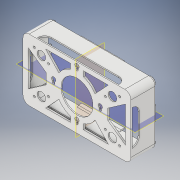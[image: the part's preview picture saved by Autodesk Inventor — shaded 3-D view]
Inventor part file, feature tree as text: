
AUTODESK INVENTOR PART (.ipt)
format: ipt  version: 2018 (Build 220112000, 112)  size: 521,216 bytes
history: native  units: in
note: dims shown in document units (in); Inventor stores cm internally (conversion verified against a paired STEP export)
features: extrude x8, sketch x8, projected_geometry x4, reference x4, other x4, plane x2, chamfer x2, mirror x2
ambient origin geometry x8: Origin, YZ Plane, XZ Plane, XY Plane, X Axis, Y Axis, Z Axis, Center Point
bodies: Solid1 (feature_tree)
feature tree (34):
  extrude  "Extrusion1"  Depth=0.0827in TaperAngle=0.0deg
  sketch  "Sketch4"  dims[d103=0.15in d104=0.0799in]
  extrude  "Extrusion12"  Depth=0.0799in
  sketch  "Sketch7"  dims[d105=0.2299in d106=1.64in]
  extrude  "Extrusion14"  Depth=1.64in
  extrude  "Extrusion16"  Depth=0.15in
  extrude  "Extrusion17"  Depth=3.28in
  plane  "Work Plane4"
  plane  "Work Plane5"
  extrude  "Extrusion23"  Depth=3.28in
  chamfer  "Chamfer2"  Distance=0.3937in
  chamfer  "Chamfer3"  Distance=1.0in
  extrude  "Extrusion24"  Depth=0.5in
  mirror  "Mirror3"
  extrude  "Extrusion25"  Depth=0.5in
  mirror  "Mirror4"
  sketch  "Sketch1"  dims[d0=0.0827in d1=1.6in d2=0.0in d98=0.0827in d99=0.0in]
  sketch  "Sketch9"  dims[d107=0.1597in d113=0.15in d114=0.0799in d115=0.2299in d116=0.1597in]
  sketch  "Sketch10"  dims[d117=1.64in d118=0.7874in d120=3.28in]
  projected_geometry  "Projected Loop5"
  reference  "Reference6"
  projected_geometry  "Projected Loop8"
  sketch  "Sketch15"  dims[d121=0.3937in d123=1.0in d125=0.7874in d127=3.28in d128=0.3937in d130=1.0in]
  reference  "Reference12"
  reference  "Reference13"
  reference  "Reference14"
  sketch  "Sketch16"  dims[d134=0.15in]
  projected_geometry  "Projected Loop11"
  sketch  "Sketch17"  dims[d135=2.0in d136=1.0in d137=0.7874in d139=4.0in d140=0.7874in d142=2.0in d145=0.15in d146=3.0in d147=1.5in d148=0.7874in d150=6.0in d151=0.7874in d153=3.0in d156=0.0827in d157=0.0in d158=2.25in d172=1.5in d173=1.75in d174=1.0in d175=0.5in d176=0.3693in d178=0.75in d179=2.5in d181=1.25in d182=0.5in d185=0.6in d186=0.5in d187=1.0in d188=0.5in d189=0.25in d190=0.0in d191=0.0in d192=0.1in d193=0.1in d194=0.1in d195=0.1in d196=0.1in d197=0.1in d198=0.0354in d199=0.0in d210=0.0827in d255=1.0in d256=0.0827in d259=0.0827in d260=3.0in d261=0.33in d262=0.0in d263=1.0in d264=0.0827in d265=0.0827in d266=0.0827in d267=0.0827in d271=0.0827in d272=0.125in d273=60.0deg d274=0.0354in d275=0.125in d276=60.0deg d277=0.5in d281=0.5in d282=0.5in d283=0.5in d284=0.25in d285=0.0in d289=0.5in d290=0.5in d291=0.5in d292=0.25in d293=0.0in]
  projected_geometry  "Projected Loop12"
  other  "<userpath>\Desktop\LocalGit\seniorproject\hardware\mechanical\Hub\Hub Assembly.iam"
  other  "Hub Assembly.iam"
  other  "Touchscreen:1"
  other  "Hub Enclosure Front (new):1"
